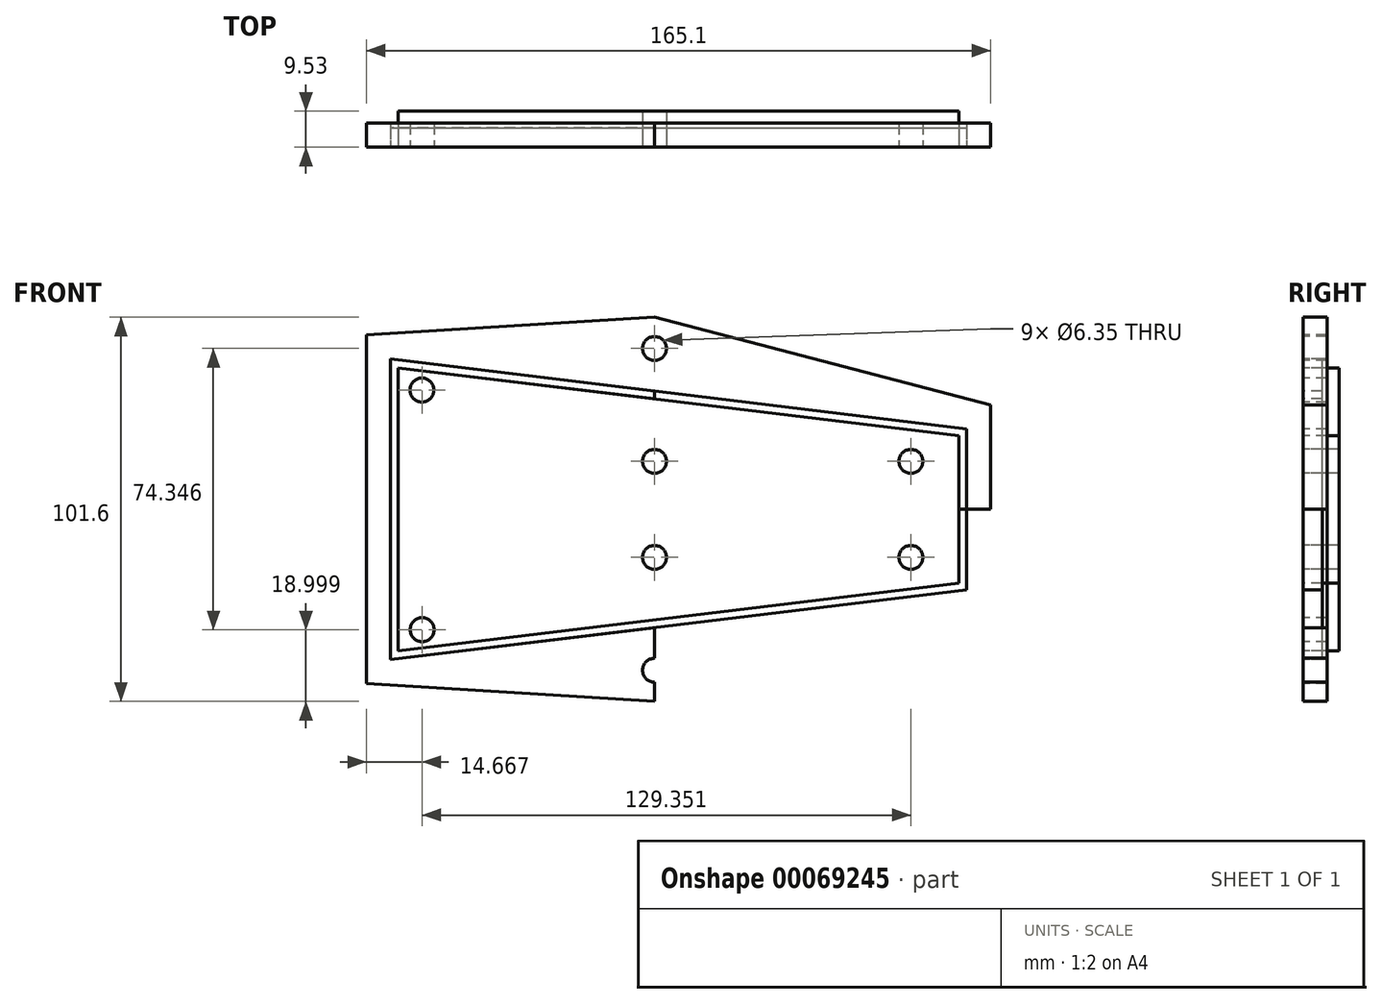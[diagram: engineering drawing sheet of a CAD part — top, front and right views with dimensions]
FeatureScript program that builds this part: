
annotation { "Feature Type Name" : "Feature", "Feature Type Description" : "" }
export const myFeature = defineFeature(function(context is Context, id is Id, definition is map)
    precondition{}
    {
        {
            var Q0;
            Q0=qCreatedBy(makeId("Front.planeOp"),FACE);
            var sketch = newSketch(context, id + "F0", { "sketchPlane" : qUnion([Q0])});
            skLineSegment(sketch, "E0", {"start": v(0, 0) * mm, "end": v(0, 50.8) * mm});
            skLineSegment(sketch, "E1", {"start": v(0, 0) * mm, "end": v(0, -50.8) * mm});
            skLineSegment(sketch, "E2", {"start": v(0, 0) * mm, "end": v(-76.2, 0) * mm});
            skLineSegment(sketch, "E3", {"start": v(0, 0) * mm, "end": v(88.9, 0) * mm});
            skLineSegment(sketch, "E4", {"start": v(88.9, 0) * mm, "end": v(88.9, -27.56) * mm});
            skLineSegment(sketch, "E5", {"start": v(88.9, -27.56) * mm, "end": v(88.9, 0) * mm});
            skLineSegment(sketch, "E6", {"start": v(88.9, 0) * mm, "end": v(88.9, 27.56) * mm});
            skLineSegment(sketch, "E7", {"start": v(-76.2, 0) * mm, "end": v(-76.2, 46.1) * mm});
            skLineSegment(sketch, "E8", {"start": v(-76.2, 0) * mm, "end": v(-76.2, -46.1) * mm});
            skLineSegment(sketch, "E9", {"start": v(88.9, 27.56) * mm, "end": v(0, 50.8) * mm});
            skLineSegment(sketch, "E10", {"start": v(0, 50.8) * mm, "end": v(-76.2, 46.1) * mm});
            skLineSegment(sketch, "E11", {"start": v(88.9, -27.56) * mm, "end": v(0, -50.8) * mm});
            skLineSegment(sketch, "E12", {"start": v(0, -50.8) * mm, "end": v(-76.2, -46.1) * mm});
            skLineSegment(sketch, "E13", {"start": v(0, 50.8) * mm, "end": v(0, 42.55) * mm});
            skLineSegment(sketch, "E14", {"start": v(0, -50.8) * mm, "end": v(0, -42.55) * mm});
            skLineSegment(sketch, "E15", {"start": v(-76.2, 0) * mm, "end": v(-69.85, 0) * mm});
            skLineSegment(sketch, "E16", {"start": v(-69.85, 0) * mm, "end": v(-69.85, 39.75) * mm});
            skLineSegment(sketch, "E17", {"start": v(-69.85, 0) * mm, "end": v(-69.85, -39.75) * mm});
            skLineSegment(sketch, "E18", {"start": v(88.9, 0) * mm, "end": v(82.55, 0) * mm});
            skLineSegment(sketch, "E19", {"start": v(82.55, 0) * mm, "end": v(82.55, 21.31) * mm});
            skLineSegment(sketch, "E20", {"start": v(82.55, 21.31) * mm, "end": v(82.55, 0) * mm});
            skLineSegment(sketch, "E21", {"start": v(82.55, -21.31) * mm, "end": v(82.55, 0) * mm});
            skLineSegment(sketch, "E22", {"start": v(82.55, 21.31) * mm, "end": v(-69.85, 39.75) * mm});
            skLineSegment(sketch, "E23", {"start": v(-69.85, -39.75) * mm, "end": v(82.55, -21.31) * mm});
            skCircle(sketch, "E24", {"center": v(0, 42.55) * mm, "radius": 3.18 * mm});
            skCircle(sketch, "E25", {"center": v(0, -42.55) * mm, "radius": 3.18 * mm});
            skLineSegment(sketch, "E26.0", {"start": v(82.3, 19.3) * mm, "end": v(-70.1, 37.73) * mm});
            skLineSegment(sketch, "E27.0", {"start": v(-70.1, -37.73) * mm, "end": v(82.3, -19.3) * mm});
            skLineSegment(sketch, "E28.0", {"start": v(-67.82, 0) * mm, "end": v(-67.82, -39.75) * mm});
            skLineSegment(sketch, "E29.0", {"start": v(-67.82, 0) * mm, "end": v(-67.82, 39.5) * mm});
            skLineSegment(sketch, "E30.0", {"start": v(80.52, 21.31) * mm, "end": v(80.52, 0) * mm});
            skLineSegment(sketch, "E31", {"start": v(-67.82, 31.57) * mm, "end": v(-61.53, 31.57) * mm});
            skLineSegment(sketch, "E32", {"start": v(-67.82, -39.75) * mm, "end": v(-67.82, -31.8) * mm});
            skLineSegment(sketch, "E33", {"start": v(-67.82, -31.8) * mm, "end": v(-61.47, -31.8) * mm});
            skCircle(sketch, "E34", {"center": v(-61.53, 31.57) * mm, "radius": 3.18 * mm});
            skCircle(sketch, "E35", {"center": v(-61.47, -31.8) * mm, "radius": 3.18 * mm});
            skCircle(sketch, "E36", {"center": v(0, 12.7) * mm, "radius": 3.18 * mm});
            skCircle(sketch, "E37", {"center": v(0, -12.7) * mm, "radius": 3.18 * mm});
            skCircle(sketch, "E38", {"center": v(67.82, 12.7) * mm, "radius": 3.18 * mm});
            skCircle(sketch, "E39", {"center": v(67.82, -12.7) * mm, "radius": 3.18 * mm});
            skPoint(sketch, "E39.centerSnap0", {"position": v(80.52, -12.7) * mm});
            skLineSegment(sketch, "E40.0", {"start": v(80.52, -21.31) * mm, "end": v(80.52, 0) * mm});
            skSolve(sketch);
        }
        {
            var Q0;
            {var subQ3=sQuery(id+"F0.wireOp",EDGE,"E26.0");var subQ5=sQuery(id+"F0.wireOp",EDGE,"E30.0");var subQ7=makeQuery(id+"F0.imprint","INTERSECT",VERTEX,{"derivedFrom":[subQ3,subQ5]});Q0=makeQuery(id+"F0.imprint","IMPRINT",FACE,{"disambiguationData":[TD([[makeQuery(id+"F0.imprint","IMPRINT",EDGE,{"disambiguationData":[TD([[subQ7,-1.0]])],"derivedFrom":subQ3}),1.0]])]});}
            var Q1;
            {var subQ1=sQuery(id+"F0.wireOp",EDGE,"E0");var subQ3=sQuery(id+"F0.wireOp",EDGE,"E26.0");var subQ4=makeQuery(id+"F0.imprint","INTERSECT",VERTEX,{"derivedFrom":[subQ1,subQ3]});Q1=makeQuery(id+"F0.imprint","IMPRINT",FACE,{"disambiguationData":[TD([[makeQuery(id+"F0.imprint","IMPRINT",EDGE,{"disambiguationData":[TD([[subQ4,-1.0]])],"derivedFrom":subQ3}),1.0]])]});}
            var Q2;
            {var subQ1=sQuery(id+"F0.wireOp",EDGE,"E1");var subQ3=sQuery(id+"F0.wireOp",EDGE,"E27.0");var subQ4=makeQuery(id+"F0.imprint","INTERSECT",VERTEX,{"derivedFrom":[subQ1,subQ3]});Q2=makeQuery(id+"F0.imprint","IMPRINT",FACE,{"disambiguationData":[TD([[makeQuery(id+"F0.imprint","IMPRINT",EDGE,{"disambiguationData":[TD([[subQ4,1.0]])],"derivedFrom":subQ3}),1.0]])]});}
            var Q3;
            Q3=makeQuery(id+"F0.imprint","IMPRINT",FACE,{"disambiguationData":[TD([[makeQuery(id+"F0.imprint","IMPRINT",EDGE,{"derivedFrom":sQuery(id+"F0.wireOp",EDGE,"E39")}),-1.0]])]});
            extrude(context, id + "F1", {"entities" : qUnion([Q0, Q1, Q2, Q3]), "oppositeDirection" : true, "depth" : 6.35 * mm});
        }
        {
            var Q0;
            Q0=makeQuery(id+"F0.imprint","IMPRINT",FACE,{"disambiguationData":[TD([[makeQuery(id+"F0.imprint","IMPRINT",EDGE,{"derivedFrom":sQuery(id+"F0.wireOp",EDGE,"E6")}),1.0]])]});
            var Q1;
            Q1=makeQuery(id+"F0.imprint","IMPRINT",FACE,{"disambiguationData":[TD([[makeQuery(id+"F0.imprint","IMPRINT",EDGE,{"derivedFrom":sQuery(id+"F0.wireOp",EDGE,"E5")}),1.0]])]});
            var Q2;
            Q2=makeQuery(id+"F0.imprint","IMPRINT",FACE,{"disambiguationData":[TD([[makeQuery(id+"F0.imprint","IMPRINT",EDGE,{"derivedFrom":sQuery(id+"F0.wireOp",EDGE,"E8")}),1.0]])]});
            var Q3;
            Q3=makeQuery(id+"F0.imprint","IMPRINT",FACE,{"disambiguationData":[TD([[makeQuery(id+"F0.imprint","IMPRINT",EDGE,{"derivedFrom":sQuery(id+"F0.wireOp",EDGE,"E7")}),-1.0]])]});
            extrude(context, id + "F2", {"entities" : qUnion([Q0, Q1, Q2, Q3]), "oppositeDirection" : true, "depth" : 6.35 * mm});
        }
        {
            var Q0;
            {var subQ0=sQuery(id+"F0.wireOp",EDGE,"E20");Q0=makeQuery(id+"F0.imprint","IMPRINT",FACE,{"disambiguationData":[TD([[makeQuery(id+"F0.imprint","IMPRINT",EDGE,{"derivedFrom":subQ0}),-1.0]])]});}
            var Q1;
            {var subQ0=sQuery(id+"F0.wireOp",EDGE,"E26.0");var subQ1=sQuery(id+"F0.wireOp",EDGE,"E0");var subQ2=makeQuery(id+"F0.imprint","INTERSECT",VERTEX,{"derivedFrom":[subQ1,subQ0]});Q1=makeQuery(id+"F0.imprint","IMPRINT",FACE,{"disambiguationData":[TD([[makeQuery(id+"F0.imprint","IMPRINT",EDGE,{"disambiguationData":[TD([[subQ2,-1.0]])],"derivedFrom":subQ1}),1.0]])]});}
            var Q2;
            {var subQ0=sQuery(id+"F0.wireOp",EDGE,"E16");var subQ5=sQuery(id+"F0.wireOp",EDGE,"E26.0");var subQ6=makeQuery(id+"F0.imprint","INTERSECT",VERTEX,{"derivedFrom":[subQ0,subQ5]});Q2=makeQuery(id+"F0.imprint","IMPRINT",FACE,{"disambiguationData":[TD([[makeQuery(id+"F0.imprint","IMPRINT",EDGE,{"disambiguationData":[TD([[subQ6,1.0]])],"derivedFrom":subQ5}),1.0]])]});}
            var Q3;
            {var subQ0=sQuery(id+"F0.wireOp",EDGE,"E22");var subQ1=sQuery(id+"F0.wireOp",EDGE,"E16");var subQ2=makeQuery(id+"F0.imprint","INTERSECT",VERTEX,{"derivedFrom":[subQ1,subQ0]});Q3=makeQuery(id+"F0.imprint","IMPRINT",FACE,{"disambiguationData":[TD([[makeQuery(id+"F0.imprint","IMPRINT",EDGE,{"disambiguationData":[TD([[subQ2,1.0]])],"derivedFrom":subQ1}),-1.0]])]});}
            var Q4;
            {var subQ0=sQuery(id+"F0.wireOp",EDGE,"E17");var subQ5=sQuery(id+"F0.wireOp",EDGE,"E27.0");var subQ6=makeQuery(id+"F0.imprint","INTERSECT",VERTEX,{"derivedFrom":[subQ0,subQ5]});Q4=makeQuery(id+"F0.imprint","IMPRINT",FACE,{"disambiguationData":[TD([[makeQuery(id+"F0.imprint","IMPRINT",EDGE,{"disambiguationData":[TD([[subQ6,-1.0]])],"derivedFrom":subQ5}),1.0]])]});}
            var Q5;
            {var subQ0=sQuery(id+"F0.wireOp",EDGE,"E23");var subQ1=sQuery(id+"F0.wireOp",EDGE,"E17");var subQ2=makeQuery(id+"F0.imprint","INTERSECT",VERTEX,{"derivedFrom":[subQ1,subQ0]});Q5=makeQuery(id+"F0.imprint","IMPRINT",FACE,{"disambiguationData":[TD([[makeQuery(id+"F0.imprint","IMPRINT",EDGE,{"disambiguationData":[TD([[subQ2,1.0]])],"derivedFrom":subQ1}),1.0]])]});}
            var Q6;
            {var subQ0=sQuery(id+"F0.wireOp",EDGE,"E27.0");var subQ1=sQuery(id+"F0.wireOp",EDGE,"E1");var subQ2=makeQuery(id+"F0.imprint","INTERSECT",VERTEX,{"derivedFrom":[subQ1,subQ0]});Q6=makeQuery(id+"F0.imprint","IMPRINT",FACE,{"disambiguationData":[TD([[makeQuery(id+"F0.imprint","IMPRINT",EDGE,{"disambiguationData":[TD([[subQ2,-1.0]])],"derivedFrom":subQ1}),-1.0]])]});}
            var Q7;
            {var subQ0=sQuery(id+"F0.wireOp",EDGE,"E21");Q7=makeQuery(id+"F0.imprint","IMPRINT",FACE,{"disambiguationData":[TD([[makeQuery(id+"F0.imprint","IMPRINT",EDGE,{"derivedFrom":subQ0}),1.0]])]});}
            extrude(context, id + "F3", {"entities" : qUnion([Q0, Q1, Q2, Q3, Q4, Q5, Q6, Q7]), "oppositeDirection" : true, "depth" : 5.08 * mm});
        }
        {
            var Q0;
            Q0=makeQuery(id+"F0.imprint","IMPRINT",FACE,{"disambiguationData":[TD([[makeQuery(id+"F0.imprint","IMPRINT",EDGE,{"derivedFrom":sQuery(id+"F0.wireOp",EDGE,"E34")}),1.0]])]});
            var Q1;
            Q1=makeQuery(id+"F0.imprint","IMPRINT",FACE,{"disambiguationData":[TD([[makeQuery(id+"F0.imprint","IMPRINT",EDGE,{"derivedFrom":sQuery(id+"F0.wireOp",EDGE,"E35")}),1.0]])]});
            var Q2;
            Q2=makeQuery(id+"F0.imprint","IMPRINT",FACE,{"disambiguationData":[TD([[makeQuery(id+"F0.imprint","IMPRINT",EDGE,{"derivedFrom":sQuery(id+"F0.wireOp",EDGE,"E39")}),1.0]])]});
            var Q3;
            {var subQ0=sQuery(id+"F0.wireOp",EDGE,"E37");var subQ1=sQuery(id+"F0.wireOp",EDGE,"E1");var subQ2=makeQuery(id+"F0.imprint","INTERSECT",VERTEX,{"disambiguationData":[OD(0.0)],"derivedFrom":[subQ1,subQ0]});Q3=makeQuery(id+"F0.imprint","IMPRINT",FACE,{"disambiguationData":[TD([[makeQuery(id+"F0.imprint","IMPRINT",EDGE,{"disambiguationData":[TD([[subQ2,-1.0]])],"derivedFrom":subQ1}),-1.0]])]});}
            var Q4;
            {var subQ0=sQuery(id+"F0.wireOp",EDGE,"E36");var subQ1=sQuery(id+"F0.wireOp",EDGE,"E0");var subQ2=makeQuery(id+"F0.imprint","INTERSECT",VERTEX,{"disambiguationData":[OD(0.0)],"derivedFrom":[subQ1,subQ0]});Q4=makeQuery(id+"F0.imprint","IMPRINT",FACE,{"disambiguationData":[TD([[makeQuery(id+"F0.imprint","IMPRINT",EDGE,{"disambiguationData":[TD([[subQ2,-1.0]])],"derivedFrom":subQ1}),-1.0]])]});}
            var Q5;
            {var subQ0=sQuery(id+"F0.wireOp",EDGE,"E36");var subQ1=sQuery(id+"F0.wireOp",EDGE,"E0");var subQ2=makeQuery(id+"F0.imprint","INTERSECT",VERTEX,{"disambiguationData":[OD(0.0)],"derivedFrom":[subQ1,subQ0]});Q5=makeQuery(id+"F0.imprint","IMPRINT",FACE,{"disambiguationData":[TD([[makeQuery(id+"F0.imprint","IMPRINT",EDGE,{"disambiguationData":[TD([[subQ2,-1.0]])],"derivedFrom":subQ1}),1.0]])]});}
            var Q6;
            {var subQ0=sQuery(id+"F0.wireOp",EDGE,"E37");var subQ1=sQuery(id+"F0.wireOp",EDGE,"E1");var subQ2=makeQuery(id+"F0.imprint","INTERSECT",VERTEX,{"disambiguationData":[OD(0.0)],"derivedFrom":[subQ1,subQ0]});Q6=makeQuery(id+"F0.imprint","IMPRINT",FACE,{"disambiguationData":[TD([[makeQuery(id+"F0.imprint","IMPRINT",EDGE,{"disambiguationData":[TD([[subQ2,-1.0]])],"derivedFrom":subQ1}),1.0]])]});}
            var Q7;
            Q7=makeQuery(id+"F0.imprint","IMPRINT",FACE,{"disambiguationData":[TD([[makeQuery(id+"F0.imprint","IMPRINT",EDGE,{"derivedFrom":sQuery(id+"F0.wireOp",EDGE,"E38")}),1.0]])]});
            extrude(context, id + "F4", {"entities" : qUnion([Q0, Q1, Q2, Q3, Q4, Q5, Q6, Q7]), "oppositeDirection" : true, "depth" : 9.52 * mm});
        }
    });
